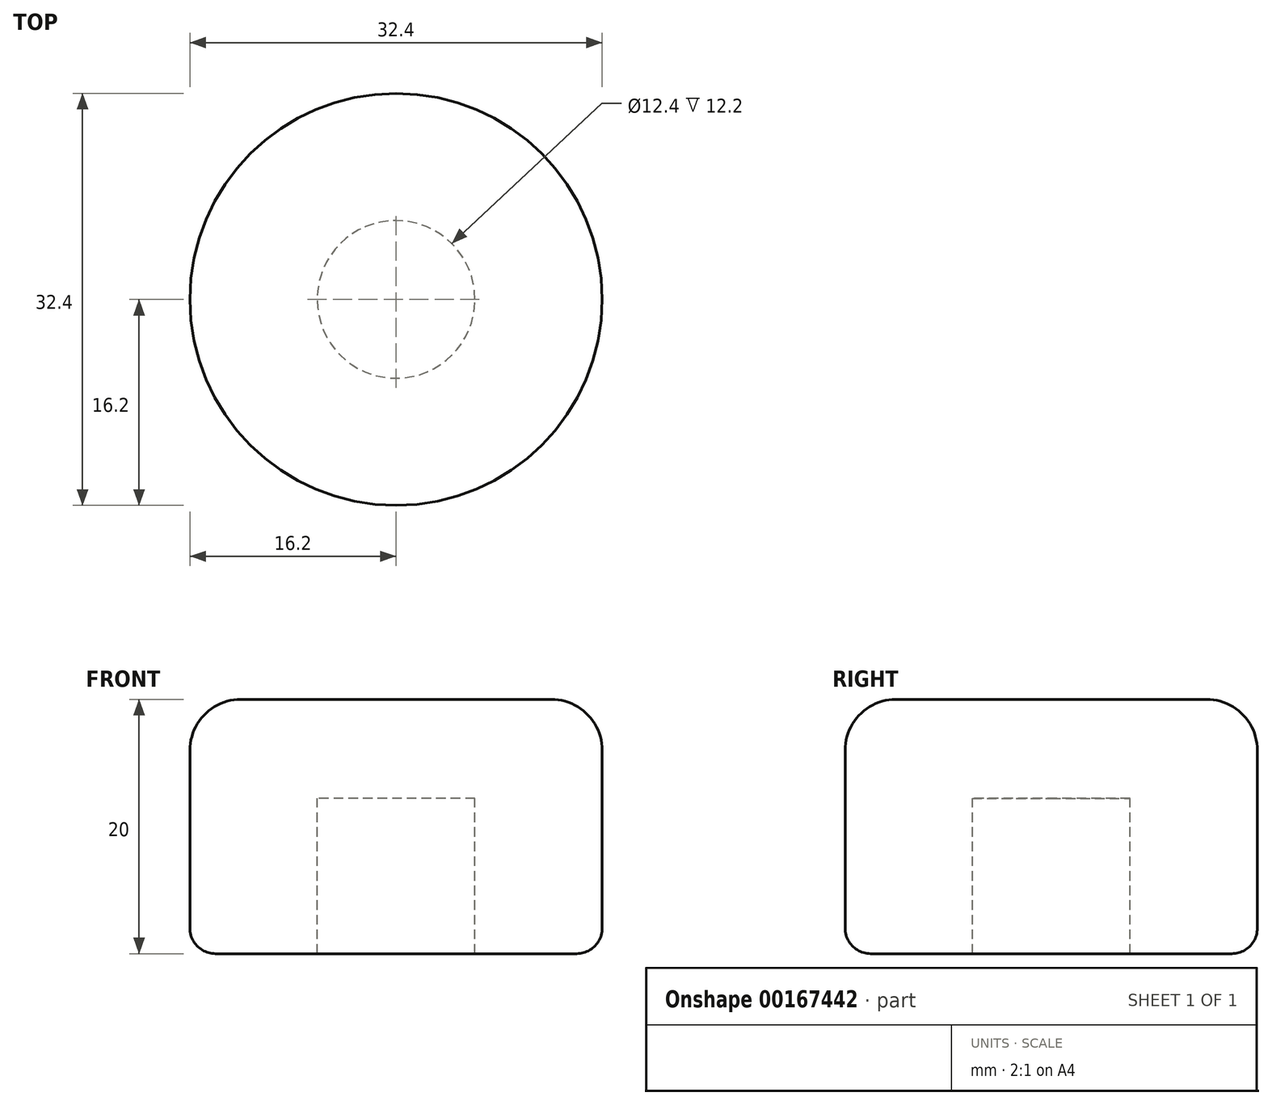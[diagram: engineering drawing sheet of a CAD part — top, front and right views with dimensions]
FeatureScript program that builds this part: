
annotation { "Feature Type Name" : "Feature", "Feature Type Description" : "" }
export const myFeature = defineFeature(function(context is Context, id is Id, definition is map)
    precondition{}
    {
        {
            var Q0;
            Q0=qCreatedBy(makeId("Front.planeOp"),FACE);
            var sketch = newSketch(context, id + "F0", { "sketchPlane" : qUnion([Q0])});
            skLineSegment(sketch, "E0.bottom", {"start": v(6.2, 6.1) * mm, "end": v(-6.2, 6.1) * mm});
            skLineSegment(sketch, "E0.left", {"start": v(6.2, 6.1) * mm, "end": v(6.2, -6.1) * mm});
            skLineSegment(sketch, "E0.right", {"start": v(-6.2, 6.1) * mm, "end": v(-6.2, -6.1) * mm});
            skPoint(sketch, "E0.middle", {"position": v(0, 0) * mm});
            skLineSegment(sketch, "E1.bottom", {"start": v(-6.2, 6.1) * mm, "end": v(-16.2, 6.1) * mm});
            skLineSegment(sketch, "E1.top", {"start": v(-6.2, -6.1) * mm, "end": v(-14.2, -6.1) * mm});
            skLineSegment(sketch, "E1.right", {"start": v(-16.2, 6.1) * mm, "end": v(-16.2, -4.1) * mm});
            skLineSegment(sketch, "E2.bottom", {"start": v(6.2, 6.1) * mm, "end": v(16.2, 6.1) * mm});
            skLineSegment(sketch, "E2.top", {"start": v(6.2, -6.1) * mm, "end": v(14.2, -6.1) * mm});
            skLineSegment(sketch, "E2.right", {"start": v(16.2, 6.1) * mm, "end": v(16.2, -4.1) * mm});
            skLineSegment(sketch, "E3.bottom", {"start": v(-16.2, 6.1) * mm, "end": v(16.2, 6.1) * mm});
            skLineSegment(sketch, "E3.top", {"start": v(-12.2, 13.9) * mm, "end": v(12.2, 13.9) * mm});
            skLineSegment(sketch, "E3.left", {"start": v(-16.2, 6.1) * mm, "end": v(-16.2, 9.9) * mm});
            skLineSegment(sketch, "E3.right", {"start": v(16.2, 6.1) * mm, "end": v(16.2, 9.9) * mm});
            skPoint(sketch, "E4.visualSharp", {"position": v(-16.2, 13.9) * mm});
            skArc(sketch, "E4.filletArc", {"start": v(-12.2, 13.9) * mm, "mid": v(-15.03, 12.73) * mm, "end": v(-16.2, 9.9) * mm});
            skPoint(sketch, "E5.visualSharp", {"position": v(16.2, 13.9) * mm});
            skArc(sketch, "E5.filletArc", {"start": v(16.2, 9.9) * mm, "mid": v(15.03, 12.73) * mm, "end": v(12.2, 13.9) * mm});
            skPoint(sketch, "E6.visualSharp", {"position": v(-16.2, -6.1) * mm});
            skArc(sketch, "E6.filletArc", {"start": v(-16.2, -4.1) * mm, "mid": v(-15.61, -5.51) * mm, "end": v(-14.2, -6.1) * mm});
            skPoint(sketch, "E7.visualSharp", {"position": v(16.2, -6.1) * mm});
            skArc(sketch, "E7.filletArc", {"start": v(14.2, -6.1) * mm, "mid": v(15.61, -5.51) * mm, "end": v(16.2, -4.1) * mm});
            skLineSegment(sketch, "E8", {"start": v(0, 13.9) * mm, "end": v(0, 6.1) * mm});
            skSolve(sketch);
        }
        {
            var Q0;
            {var subQ0=sQuery(id+"F0.wireOp",EDGE,"E3.left");Q0=makeQuery(id+"F0.imprint","IMPRINT",FACE,{"disambiguationData":[TD([[makeQuery(id+"F0.imprint","IMPRINT",EDGE,{"derivedFrom":subQ0}),-1.0]])]});}
            var Q1;
            Q1=makeQuery(id+"F0.imprint","IMPRINT",FACE,{"disambiguationData":[TD([[makeQuery(id+"F0.imprint","IMPRINT",EDGE,{"derivedFrom":sQuery(id+"F0.wireOp",EDGE,"E1.top")}),-1.0]])]});
            var Q2;
            Q2=sQuery(id+"F0.wireOp",EDGE,"E8");
            revolve(context, id + "F1", {"entities" : qUnion([Q0, Q1]), "axis" : qUnion([Q2]), "revolveType" : RevolveType.FULL});
        }
    });
